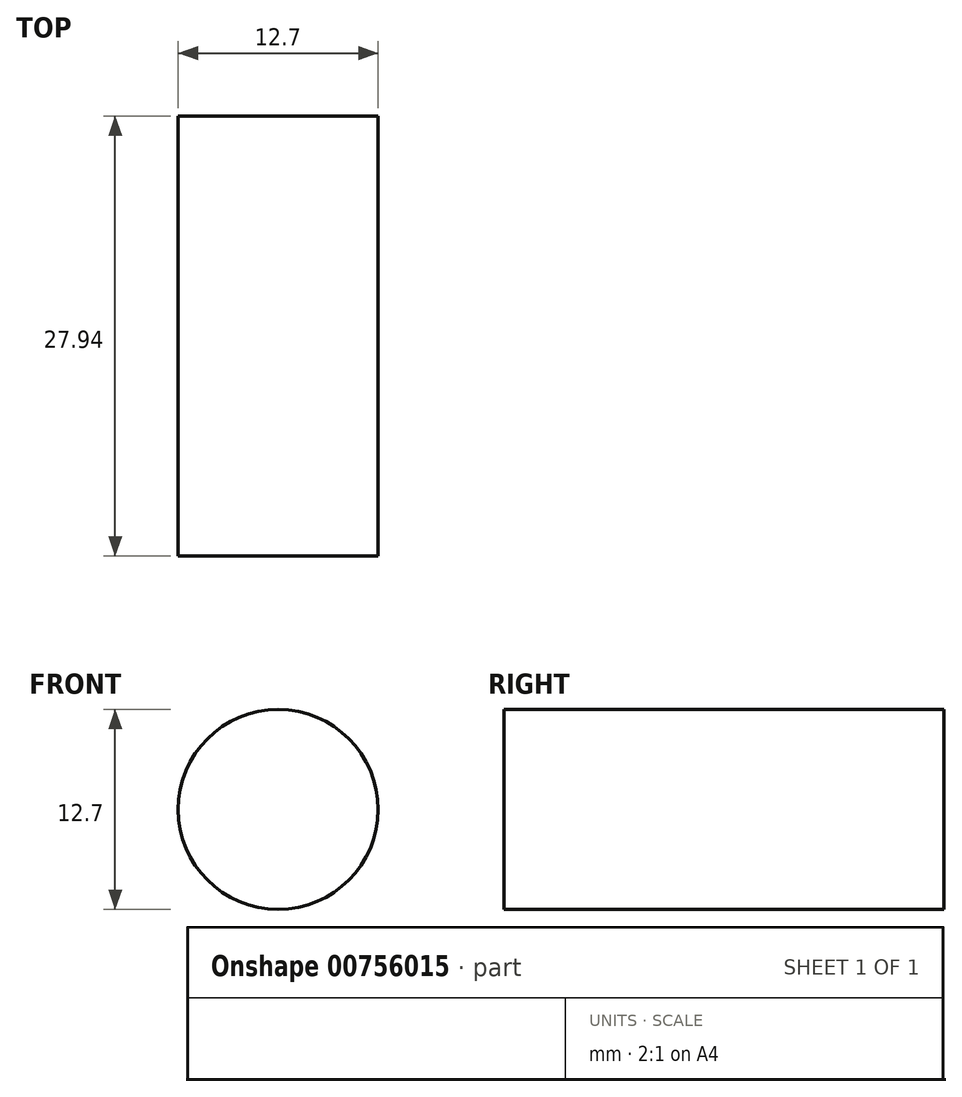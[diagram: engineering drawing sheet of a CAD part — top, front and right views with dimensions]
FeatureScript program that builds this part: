
annotation { "Feature Type Name" : "Feature", "Feature Type Description" : "" }
export const myFeature = defineFeature(function(context is Context, id is Id, definition is map)
    precondition{}
    {
        {
            var Q0;
            Q0=qCreatedBy(makeId("Front.planeOp"),FACE);
            var sketch = newSketch(context, id + "F0", { "sketchPlane" : qUnion([Q0])});
            skCircle(sketch, "E0", {"center": v(0, 0) * mm, "radius": 6.35 * mm});
            skSolve(sketch);
        }
        {
            var Q0;
            Q0=makeQuery(id+"F0.imprint","IMPRINT",FACE,{"disambiguationData":[TD([[makeQuery(id+"F0.imprint","IMPRINT",EDGE,{"derivedFrom":sQuery(id+"F0.wireOp",EDGE,"E0")}),1.0]])]});
            extrude(context, id + "F1", {"entities" : qUnion([Q0]), "depth" : 27.94 * mm, "offsetDistance" : 25.4 * mm});
        }
    });
